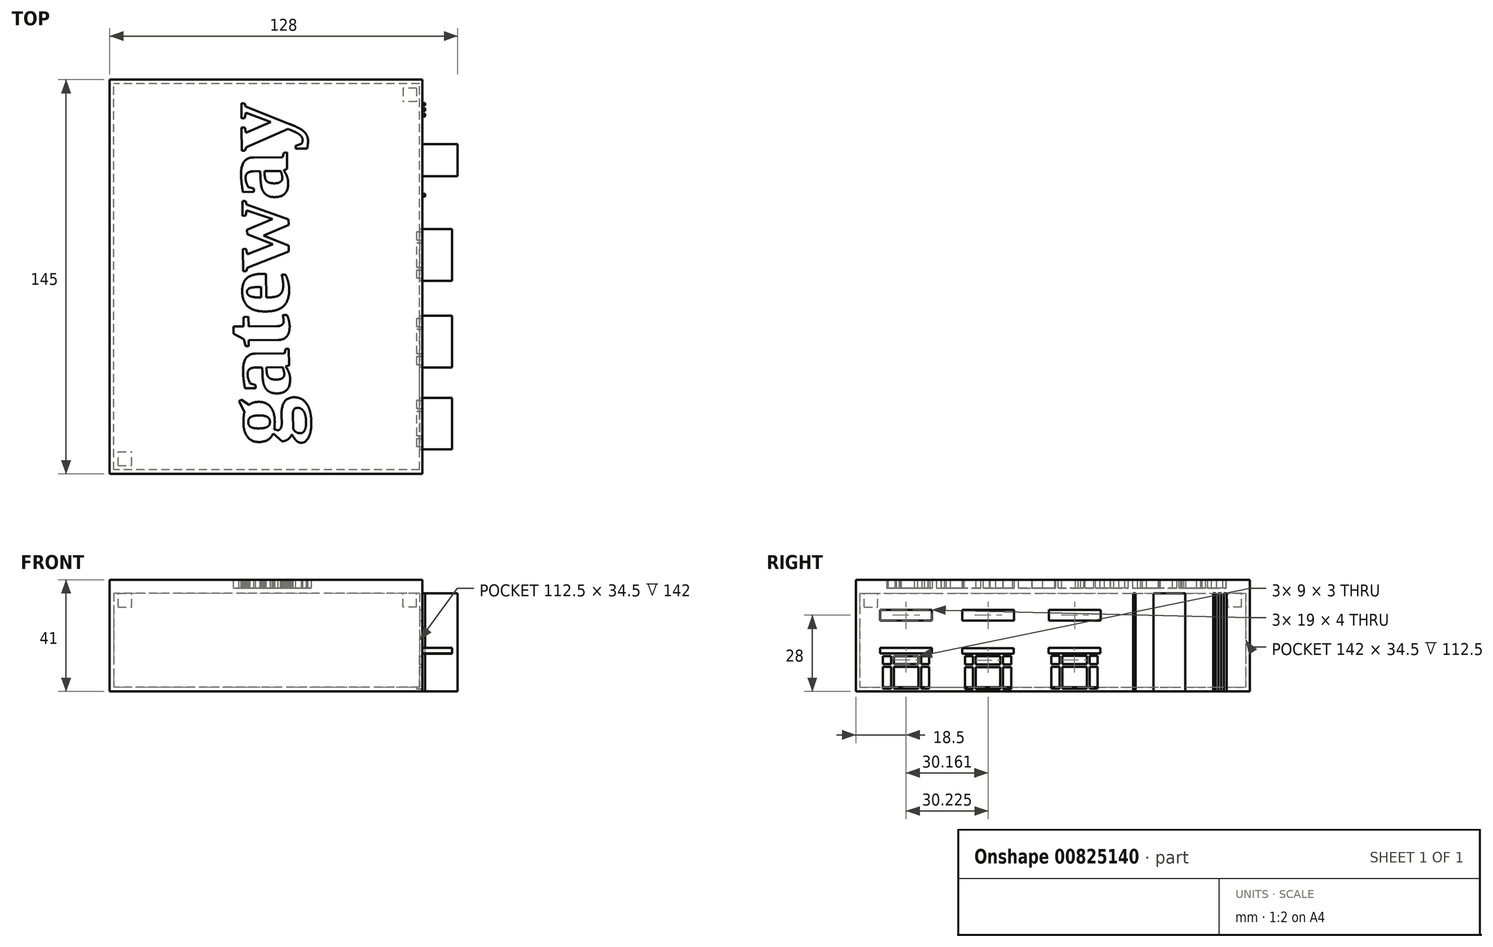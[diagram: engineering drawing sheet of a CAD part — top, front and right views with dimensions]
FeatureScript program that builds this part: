
annotation { "Feature Type Name" : "Feature", "Feature Type Description" : "" }
export const myFeature = defineFeature(function(context is Context, id is Id, definition is map)
    precondition{}
    {
        {
            var Q0;
            Q0=qCreatedBy(makeId("Top.planeOp"),FACE);
            var sketch = newSketch(context, id + "F0", { "sketchPlane" : qUnion([Q0])});
            skLineSegment(sketch, "E0.bottom", {"start": v(0, 0) * mm, "end": v(-116, 0) * mm});
            skLineSegment(sketch, "E0.top", {"start": v(0, 145) * mm, "end": v(-116, 145) * mm});
            skLineSegment(sketch, "E0.left", {"start": v(0, 0) * mm, "end": v(0, 145) * mm});
            skLineSegment(sketch, "E0.right", {"start": v(-116, 0) * mm, "end": v(-116, 145) * mm});
            skSolve(sketch);
        }
        {
            var Q0;
            Q0=makeQuery(id+"F0.imprint","IMPRINT",FACE,{"disambiguationData":[TD([[makeQuery(id+"F0.imprint","IMPRINT",EDGE,{"derivedFrom":sQuery(id+"F0.wireOp",EDGE,"E0.bottom")}),-1.0]])]});
            extrude(context, id + "F1", {"entities" : qUnion([Q0]), "depth" : 36 * mm, "offsetDistance" : 25 * mm});
        }
        {
            var Q0;
            Q0=makeQuery(id+"F1.opExtrude","CAP_FACE",FACE,{"disambiguationData":[OSD([sQuery(id+"F0.wireOp",EDGE,"E0.bottom"),sQuery(id+"F0.wireOp",EDGE,"E0.top"),sQuery(id+"F0.wireOp",EDGE,"E0.left"),sQuery(id+"F0.wireOp",EDGE,"E0.right")])],"isStart":false});
            shell(context, id + "F2", {"entities" : qUnion([Q0]), "thickness" : 3 * mm});
        }
        {
            var Q0;
            Q0=makeQuery(id+"F1.opExtrude","CAP_FACE",FACE,{"disambiguationData":[OSD([sQuery(id+"F0.wireOp",EDGE,"E0.bottom"),sQuery(id+"F0.wireOp",EDGE,"E0.top"),sQuery(id+"F0.wireOp",EDGE,"E0.left"),sQuery(id+"F0.wireOp",EDGE,"E0.right")])],"isStart":false});
            var sketch = newSketch(context, id + "F3", { "sketchPlane" : qUnion([Q0])});
            skLineSegment(sketch, "E1.bottom", {"start": v(-116, 0) * mm, "end": v(0, 0) * mm});
            skLineSegment(sketch, "E1.top", {"start": v(-116, 145) * mm, "end": v(0, 145) * mm});
            skLineSegment(sketch, "E1.left", {"start": v(-116, 0) * mm, "end": v(-116, 145) * mm});
            skLineSegment(sketch, "E1.right", {"start": v(0, 0) * mm, "end": v(0, 145) * mm});
            skSolve(sketch);
        }
        {
            var Q0;
            Q0 = qSketchRegion(id + "F3", true);
            extrude(context, id + "F4", {"entities" : qUnion([Q0]), "depth" : 5 * mm, "offsetDistance" : 25 * mm});
        }
        {
            var Q0;
            Q0=makeQuery(id+"F4.opExtrude","CAP_FACE",FACE,{"disambiguationData":[OSD([sQuery(id+"F3.wireOp",EDGE,"E1.bottom"),sQuery(id+"F3.wireOp",EDGE,"E1.top"),sQuery(id+"F3.wireOp",EDGE,"E1.left"),sQuery(id+"F3.wireOp",EDGE,"E1.right")])],"isStart":false});
            var sketch = newSketch(context, id + "F5", { "sketchPlane" : qUnion([Q0])});
            skLineSegment(sketch, "E2.bottom", {"start": v(-112.9, 3.1) * mm, "end": v(-107.9, 3.1) * mm});
            skLineSegment(sketch, "E2.top", {"start": v(-112.9, 8.1) * mm, "end": v(-107.9, 8.1) * mm});
            skLineSegment(sketch, "E2.left", {"start": v(-112.9, 3.1) * mm, "end": v(-112.9, 8.1) * mm});
            skLineSegment(sketch, "E2.right", {"start": v(-107.9, 3.1) * mm, "end": v(-107.9, 8.1) * mm});
            skSolve(sketch);
        }
        {
            var Q0;
            Q0 = qSketchRegion(id + "F5", true);
            extrude(context, id + "F6", {"entities" : qUnion([Q0]), "operationType" : NewBodyOperationType.ADD, "oppositeDirection" : true, "depth" : 10 * mm, "offsetDistance" : 25 * mm});
        }
        {
            var Q0;
            Q0=makeQuery(id+"F4.opExtrude","CAP_FACE",FACE,{"disambiguationData":[OSD([sQuery(id+"F3.wireOp",EDGE,"E1.bottom"),sQuery(id+"F3.wireOp",EDGE,"E1.top"),sQuery(id+"F3.wireOp",EDGE,"E1.left"),sQuery(id+"F3.wireOp",EDGE,"E1.right")])],"isStart":false});
            var sketch = newSketch(context, id + "F7", { "sketchPlane" : qUnion([Q0])});
            skLineSegment(sketch, "E3.bottom", {"start": v(-3.1, 141.9) * mm, "end": v(-8.1, 141.9) * mm});
            skLineSegment(sketch, "E3.top", {"start": v(-3.1, 136.9) * mm, "end": v(-8.1, 136.9) * mm});
            skLineSegment(sketch, "E3.left", {"start": v(-3.1, 141.9) * mm, "end": v(-3.1, 136.9) * mm});
            skLineSegment(sketch, "E3.right", {"start": v(-8.1, 141.9) * mm, "end": v(-8.1, 136.9) * mm});
            skSolve(sketch);
        }
        {
            var Q0;
            Q0 = qSketchRegion(id + "F7", true);
            extrude(context, id + "F8", {"entities" : qUnion([Q0]), "operationType" : NewBodyOperationType.ADD, "oppositeDirection" : true, "depth" : 10 * mm, "offsetDistance" : 25 * mm});
        }
        {
            var Q0;
            Q0=makeQuery(id+"F4.opExtrude","CAP_FACE",FACE,{"disambiguationData":[OSD([sQuery(id+"F3.wireOp",EDGE,"E1.bottom"),sQuery(id+"F3.wireOp",EDGE,"E1.top"),sQuery(id+"F3.wireOp",EDGE,"E1.left"),sQuery(id+"F3.wireOp",EDGE,"E1.right")])],"isStart":false});
            var sketch = newSketch(context, id + "F9", { "sketchPlane" : qUnion([Q0])});
            skText(sketch, "E4", { "text": "gateway", "fontName": "Tinos-Bold.ttf"});
            const initialGuessF9  = {"E4": [-0.04971, 0.01043, -0.01004, 0.99995, 0.026]};
            skSetInitialGuess(sketch, initialGuessF9);
            skSolve(sketch);
        }
        {
            var Q0;
            Q0 = qSketchRegion(id + "F9", true);
            extrude(context, id + "F10", {"entities" : qUnion([Q0]), "operationType" : NewBodyOperationType.REMOVE, "oppositeDirection" : true, "depth" : 3 * mm, "offsetDistance" : 25 * mm});
        }
        {
            var Q0;
            Q0=makeQuery(id+"F1.opExtrude","SWEPT_FACE",FACE,{"disambiguationData":[OSD([sQuery(id+"F0.wireOp",EDGE,"E0.left")])]});
            var sketch = newSketch(context, id + "F11", { "sketchPlane" : qUnion([Q0])});
            skLineSegment(sketch, "E5.bottom", {"start": v(115, 0) * mm, "end": v(125, 0) * mm});
            skLineSegment(sketch, "E5.top", {"start": v(115, 36) * mm, "end": v(125, 36) * mm});
            skLineSegment(sketch, "E5.left", {"start": v(115, 0) * mm, "end": v(115, 36) * mm});
            skLineSegment(sketch, "E5.right", {"start": v(125, 0) * mm, "end": v(125, 36) * mm});
            skLineSegment(sketch, "E6.bottom", {"start": v(1, 0) * mm, "end": v(2, 0) * mm});
            skLineSegment(sketch, "E6.top", {"start": v(1, 36) * mm, "end": v(2, 36) * mm});
            skLineSegment(sketch, "E6.left", {"start": v(1, 0) * mm, "end": v(1, 36) * mm});
            skLineSegment(sketch, "E6.right", {"start": v(2, 0) * mm, "end": v(2, 36) * mm});
            skLineSegment(sketch, "E7.bottom", {"start": v(3, 0) * mm, "end": v(4, 0) * mm});
            skLineSegment(sketch, "E7.top", {"start": v(3, 36) * mm, "end": v(4, 36) * mm});
            skLineSegment(sketch, "E7.left", {"start": v(3, 0) * mm, "end": v(3, 36) * mm});
            skLineSegment(sketch, "E7.right", {"start": v(4, 0) * mm, "end": v(4, 36) * mm});
            skLineSegment(sketch, "E8.bottom", {"start": v(5, 0) * mm, "end": v(6, 0) * mm});
            skLineSegment(sketch, "E8.top", {"start": v(5, 36) * mm, "end": v(6, 36) * mm});
            skLineSegment(sketch, "E8.left", {"start": v(5, 0) * mm, "end": v(5, 36) * mm});
            skLineSegment(sketch, "E8.right", {"start": v(6, 0) * mm, "end": v(6, 36) * mm});
            skLineSegment(sketch, "E9.bottom", {"start": v(7, 0) * mm, "end": v(8, 0) * mm});
            skLineSegment(sketch, "E9.top", {"start": v(7, 36) * mm, "end": v(8, 36) * mm});
            skLineSegment(sketch, "E9.left", {"start": v(7, 0) * mm, "end": v(7, 36) * mm});
            skLineSegment(sketch, "E9.right", {"start": v(8, 0) * mm, "end": v(8, 36) * mm});
            skSolve(sketch);
        }
        {
            var Q0;
            Q0=makeQuery(id+"F11.imprint","IMPRINT",FACE,{"disambiguationData":[TD([[makeQuery(id+"F11.imprint","IMPRINT",EDGE,{"derivedFrom":sQuery(id+"F11.wireOp",EDGE,"E6.bottom")}),1.0]])]});
            var Q1;
            Q1=makeQuery(id+"F11.imprint","IMPRINT",FACE,{"disambiguationData":[TD([[makeQuery(id+"F11.imprint","IMPRINT",EDGE,{"derivedFrom":sQuery(id+"F11.wireOp",EDGE,"E7.bottom")}),1.0]])]});
            var Q2;
            Q2=makeQuery(id+"F11.imprint","IMPRINT",FACE,{"disambiguationData":[TD([[makeQuery(id+"F11.imprint","IMPRINT",EDGE,{"derivedFrom":sQuery(id+"F11.wireOp",EDGE,"E8.bottom")}),1.0]])]});
            var Q3;
            Q3=makeQuery(id+"F11.imprint","IMPRINT",FACE,{"disambiguationData":[TD([[makeQuery(id+"F11.imprint","IMPRINT",EDGE,{"derivedFrom":sQuery(id+"F11.wireOp",EDGE,"E9.bottom")}),1.0]])]});
            extrude(context, id + "F12", {"entities" : qUnion([Q0, Q1, Q2, Q3]), "operationType" : NewBodyOperationType.REMOVE, "oppositeDirection" : true, "depth" : 1 * mm, "offsetDistance" : 25 * mm});
        }
        {
            var Q0;
            {var subQ1=sQuery(id+"F0.wireOp",EDGE,"E0.left");var subQ2=sQuery(id+"F0.wireOp",EDGE,"E0.top");Q0=makeQuery(id+"F12.boolean.opBoolean","SPLIT",FACE,{"disambiguationData":[TD([makeQuery(id+"F1.opExtrude","SWEPT_FACE",FACE,{"disambiguationData":[OSD([subQ2])]})])],"derivedFrom":makeQuery(id+"F1.opExtrude","SWEPT_FACE",FACE,{"disambiguationData":[OSD([subQ1])]})});}
            var sketch = newSketch(context, id + "F13", { "sketchPlane" : qUnion([Q0])});
            skLineSegment(sketch, "E10.bottom", {"start": v(10, 1) * mm, "end": v(13, 1) * mm});
            skLineSegment(sketch, "E10.top", {"start": v(10, 9) * mm, "end": v(13, 9) * mm});
            skLineSegment(sketch, "E10.left", {"start": v(10, 1) * mm, "end": v(10, 9) * mm});
            skLineSegment(sketch, "E10.right", {"start": v(13, 1) * mm, "end": v(13, 9) * mm});
            skLineSegment(sketch, "E11.bottom", {"start": v(10, 10) * mm, "end": v(13, 10) * mm});
            skLineSegment(sketch, "E11.top", {"start": v(10, 13) * mm, "end": v(13, 13) * mm});
            skLineSegment(sketch, "E11.left", {"start": v(10, 10) * mm, "end": v(10, 13) * mm});
            skLineSegment(sketch, "E11.right", {"start": v(13, 10) * mm, "end": v(13, 13) * mm});
            skLineSegment(sketch, "E12.bottom", {"start": v(14, 1) * mm, "end": v(23, 1) * mm});
            skLineSegment(sketch, "E12.top", {"start": v(14, 9) * mm, "end": v(23, 9) * mm});
            skLineSegment(sketch, "E12.left", {"start": v(14, 1) * mm, "end": v(14, 9) * mm});
            skLineSegment(sketch, "E12.right", {"start": v(23, 1) * mm, "end": v(23, 9) * mm});
            skLineSegment(sketch, "E13.bottom", {"start": v(23, 10) * mm, "end": v(14, 10) * mm});
            skLineSegment(sketch, "E13.top", {"start": v(23, 13) * mm, "end": v(14, 13) * mm});
            skLineSegment(sketch, "E13.left", {"start": v(23, 10) * mm, "end": v(23, 13) * mm});
            skLineSegment(sketch, "E13.right", {"start": v(14, 10) * mm, "end": v(14, 13) * mm});
            skLineSegment(sketch, "E14.bottom", {"start": v(24, 1) * mm, "end": v(27, 1) * mm});
            skLineSegment(sketch, "E14.top", {"start": v(24, 9) * mm, "end": v(27, 9) * mm});
            skLineSegment(sketch, "E14.left", {"start": v(24, 1) * mm, "end": v(24, 9) * mm});
            skLineSegment(sketch, "E14.right", {"start": v(27, 1) * mm, "end": v(27, 9) * mm});
            skLineSegment(sketch, "E15.bottom", {"start": v(24, 10) * mm, "end": v(27, 10) * mm});
            skLineSegment(sketch, "E15.top", {"start": v(24, 13) * mm, "end": v(27, 13) * mm});
            skLineSegment(sketch, "E15.left", {"start": v(24, 10) * mm, "end": v(24, 13) * mm});
            skLineSegment(sketch, "E15.right", {"start": v(27, 10) * mm, "end": v(27, 13) * mm});
            skLineSegment(sketch, "E16.bottom", {"start": v(9, 14) * mm, "end": v(28, 14) * mm});
            skLineSegment(sketch, "E16.top", {"start": v(9, 16) * mm, "end": v(28, 16) * mm});
            skLineSegment(sketch, "E16.left", {"start": v(9, 14) * mm, "end": v(9, 16) * mm});
            skLineSegment(sketch, "E16.right", {"start": v(28, 14) * mm, "end": v(28, 16) * mm});
            skLineSegment(sketch, "E17.bottom", {"start": v(40.16, 0.88) * mm, "end": v(43.16, 0.88) * mm});
            skLineSegment(sketch, "E17.top", {"start": v(40.16, 8.88) * mm, "end": v(43.16, 8.88) * mm});
            skLineSegment(sketch, "E17.left", {"start": v(40.16, 0.88) * mm, "end": v(40.16, 8.88) * mm});
            skLineSegment(sketch, "E17.right", {"start": v(43.16, 0.88) * mm, "end": v(43.16, 8.88) * mm});
            skLineSegment(sketch, "E18.bottom", {"start": v(40.16, 9.88) * mm, "end": v(43.16, 9.88) * mm});
            skLineSegment(sketch, "E18.top", {"start": v(40.16, 12.88) * mm, "end": v(43.16, 12.88) * mm});
            skLineSegment(sketch, "E18.left", {"start": v(40.16, 9.88) * mm, "end": v(40.16, 12.88) * mm});
            skLineSegment(sketch, "E18.right", {"start": v(43.16, 9.88) * mm, "end": v(43.16, 12.88) * mm});
            skLineSegment(sketch, "E19.bottom", {"start": v(44.16, 0.88) * mm, "end": v(53.16, 0.88) * mm});
            skLineSegment(sketch, "E19.top", {"start": v(44.16, 8.89) * mm, "end": v(53.16, 8.89) * mm});
            skLineSegment(sketch, "E19.left", {"start": v(44.16, 0.88) * mm, "end": v(44.16, 8.89) * mm});
            skLineSegment(sketch, "E19.right", {"start": v(53.16, 0.88) * mm, "end": v(53.16, 8.89) * mm});
            skLineSegment(sketch, "E20.bottom", {"start": v(53.16, 9.88) * mm, "end": v(44.16, 9.88) * mm});
            skLineSegment(sketch, "E20.top", {"start": v(53.16, 12.88) * mm, "end": v(44.16, 12.88) * mm});
            skLineSegment(sketch, "E20.left", {"start": v(53.16, 9.88) * mm, "end": v(53.16, 12.88) * mm});
            skLineSegment(sketch, "E20.right", {"start": v(44.16, 9.88) * mm, "end": v(44.16, 12.88) * mm});
            skLineSegment(sketch, "E21.bottom", {"start": v(54.16, 0.88) * mm, "end": v(57.19, 0.88) * mm});
            skLineSegment(sketch, "E21.top", {"start": v(54.16, 8.88) * mm, "end": v(57.19, 8.88) * mm});
            skLineSegment(sketch, "E21.left", {"start": v(54.16, 0.88) * mm, "end": v(54.16, 8.88) * mm});
            skLineSegment(sketch, "E21.right", {"start": v(57.19, 0.88) * mm, "end": v(57.19, 8.88) * mm});
            skLineSegment(sketch, "E22.bottom", {"start": v(54.16, 9.88) * mm, "end": v(57.16, 9.88) * mm});
            skLineSegment(sketch, "E22.top", {"start": v(54.16, 12.88) * mm, "end": v(57.16, 12.88) * mm});
            skLineSegment(sketch, "E22.left", {"start": v(54.16, 9.88) * mm, "end": v(54.16, 12.88) * mm});
            skLineSegment(sketch, "E22.right", {"start": v(57.16, 9.88) * mm, "end": v(57.16, 12.88) * mm});
            skLineSegment(sketch, "E23.bottom", {"start": v(39.16, 13.88) * mm, "end": v(58.16, 13.88) * mm});
            skLineSegment(sketch, "E23.top", {"start": v(39.16, 15.88) * mm, "end": v(58.16, 15.88) * mm});
            skLineSegment(sketch, "E23.left", {"start": v(39.16, 13.88) * mm, "end": v(39.16, 15.88) * mm});
            skLineSegment(sketch, "E23.right", {"start": v(58.16, 13.88) * mm, "end": v(58.16, 15.88) * mm});
            skLineSegment(sketch, "E24.bottom", {"start": v(71.98, 1.01) * mm, "end": v(74.98, 1.01) * mm});
            skLineSegment(sketch, "E24.top", {"start": v(71.98, 9.01) * mm, "end": v(74.98, 9.01) * mm});
            skLineSegment(sketch, "E24.left", {"start": v(71.98, 1.01) * mm, "end": v(71.98, 9.01) * mm});
            skLineSegment(sketch, "E24.right", {"start": v(74.98, 1.01) * mm, "end": v(74.98, 9.01) * mm});
            skLineSegment(sketch, "E25.bottom", {"start": v(71.98, 10.01) * mm, "end": v(74.98, 10.01) * mm});
            skLineSegment(sketch, "E25.top", {"start": v(71.98, 13.01) * mm, "end": v(74.98, 13.01) * mm});
            skLineSegment(sketch, "E25.left", {"start": v(71.98, 10.01) * mm, "end": v(71.98, 13.01) * mm});
            skLineSegment(sketch, "E25.right", {"start": v(74.98, 10.01) * mm, "end": v(74.98, 13.01) * mm});
            skLineSegment(sketch, "E26.bottom", {"start": v(75.98, 1.01) * mm, "end": v(84.98, 1.01) * mm});
            skLineSegment(sketch, "E26.top", {"start": v(75.98, 9.02) * mm, "end": v(84.98, 9.02) * mm});
            skLineSegment(sketch, "E26.left", {"start": v(75.98, 1.01) * mm, "end": v(75.98, 9.02) * mm});
            skLineSegment(sketch, "E26.right", {"start": v(84.98, 1.01) * mm, "end": v(84.98, 9.02) * mm});
            skLineSegment(sketch, "E27.bottom", {"start": v(84.98, 10.01) * mm, "end": v(75.98, 10.01) * mm});
            skLineSegment(sketch, "E27.top", {"start": v(84.98, 13.01) * mm, "end": v(75.98, 13.01) * mm});
            skLineSegment(sketch, "E27.left", {"start": v(84.98, 10.01) * mm, "end": v(84.98, 13.01) * mm});
            skLineSegment(sketch, "E27.right", {"start": v(75.98, 10.01) * mm, "end": v(75.98, 13.01) * mm});
            skLineSegment(sketch, "E28.bottom", {"start": v(85.98, 1.01) * mm, "end": v(89.01, 1.01) * mm});
            skLineSegment(sketch, "E28.top", {"start": v(85.98, 9.01) * mm, "end": v(89.01, 9.01) * mm});
            skLineSegment(sketch, "E28.left", {"start": v(85.98, 1.01) * mm, "end": v(85.98, 9.01) * mm});
            skLineSegment(sketch, "E28.right", {"start": v(89.01, 1.01) * mm, "end": v(89.01, 9.01) * mm});
            skLineSegment(sketch, "E29.bottom", {"start": v(85.98, 10.01) * mm, "end": v(88.98, 10.01) * mm});
            skLineSegment(sketch, "E29.top", {"start": v(85.98, 13.01) * mm, "end": v(88.98, 13.01) * mm});
            skLineSegment(sketch, "E29.left", {"start": v(85.98, 10.01) * mm, "end": v(85.98, 13.01) * mm});
            skLineSegment(sketch, "E29.right", {"start": v(88.98, 10.01) * mm, "end": v(88.98, 13.01) * mm});
            skLineSegment(sketch, "E30.bottom", {"start": v(70.98, 14.01) * mm, "end": v(89.98, 14.01) * mm});
            skLineSegment(sketch, "E30.top", {"start": v(70.98, 16.01) * mm, "end": v(89.98, 16.01) * mm});
            skLineSegment(sketch, "E30.left", {"start": v(70.98, 14.01) * mm, "end": v(70.98, 16.01) * mm});
            skLineSegment(sketch, "E30.right", {"start": v(89.98, 14.01) * mm, "end": v(89.98, 16.01) * mm});
            skLineSegment(sketch, "E31.bottom", {"start": v(109.5, 0) * mm, "end": v(121.28, 0) * mm});
            skLineSegment(sketch, "E31.top", {"start": v(109.5, 36) * mm, "end": v(121.28, 36) * mm});
            skLineSegment(sketch, "E31.left", {"start": v(109.5, 0) * mm, "end": v(109.5, 36) * mm});
            skLineSegment(sketch, "E31.right", {"start": v(121.28, 0) * mm, "end": v(121.28, 36) * mm});
            skSolve(sketch);
        }
        {
            var Q0;
            Q0=makeQuery(id+"F13.imprint","IMPRINT",FACE,{"disambiguationData":[TD([[makeQuery(id+"F13.imprint","IMPRINT",EDGE,{"derivedFrom":sQuery(id+"F13.wireOp",EDGE,"E11.bottom")}),1.0]])]});
            var Q1;
            Q1=makeQuery(id+"F13.imprint","IMPRINT",FACE,{"disambiguationData":[TD([[makeQuery(id+"F13.imprint","IMPRINT",EDGE,{"derivedFrom":sQuery(id+"F13.wireOp",EDGE,"E13.bottom")}),-1.0]])]});
            var Q2;
            Q2=makeQuery(id+"F13.imprint","IMPRINT",FACE,{"disambiguationData":[TD([[makeQuery(id+"F13.imprint","IMPRINT",EDGE,{"derivedFrom":sQuery(id+"F13.wireOp",EDGE,"E15.bottom")}),1.0]])]});
            var Q3;
            Q3=makeQuery(id+"F13.imprint","IMPRINT",FACE,{"disambiguationData":[TD([[makeQuery(id+"F13.imprint","IMPRINT",EDGE,{"derivedFrom":sQuery(id+"F13.wireOp",EDGE,"E14.bottom")}),1.0]])]});
            var Q4;
            Q4=makeQuery(id+"F13.imprint","IMPRINT",FACE,{"disambiguationData":[TD([[makeQuery(id+"F13.imprint","IMPRINT",EDGE,{"derivedFrom":sQuery(id+"F13.wireOp",EDGE,"E12.bottom")}),1.0]])]});
            var Q5;
            Q5=makeQuery(id+"F13.imprint","IMPRINT",FACE,{"disambiguationData":[TD([[makeQuery(id+"F13.imprint","IMPRINT",EDGE,{"derivedFrom":sQuery(id+"F13.wireOp",EDGE,"E10.bottom")}),1.0]])]});
            var Q6;
            Q6=makeQuery(id+"F13.imprint","IMPRINT",FACE,{"disambiguationData":[TD([[makeQuery(id+"F13.imprint","IMPRINT",EDGE,{"derivedFrom":sQuery(id+"F13.wireOp",EDGE,"E18.bottom")}),1.0]])]});
            var Q7;
            Q7=makeQuery(id+"F13.imprint","IMPRINT",FACE,{"disambiguationData":[TD([[makeQuery(id+"F13.imprint","IMPRINT",EDGE,{"derivedFrom":sQuery(id+"F13.wireOp",EDGE,"E20.bottom")}),-1.0]])]});
            var Q8;
            Q8=makeQuery(id+"F13.imprint","IMPRINT",FACE,{"disambiguationData":[TD([[makeQuery(id+"F13.imprint","IMPRINT",EDGE,{"derivedFrom":sQuery(id+"F13.wireOp",EDGE,"E22.bottom")}),1.0]])]});
            var Q9;
            Q9=makeQuery(id+"F13.imprint","IMPRINT",FACE,{"disambiguationData":[TD([[makeQuery(id+"F13.imprint","IMPRINT",EDGE,{"derivedFrom":sQuery(id+"F13.wireOp",EDGE,"E21.bottom")}),1.0]])]});
            var Q10;
            Q10=makeQuery(id+"F13.imprint","IMPRINT",FACE,{"disambiguationData":[TD([[makeQuery(id+"F13.imprint","IMPRINT",EDGE,{"derivedFrom":sQuery(id+"F13.wireOp",EDGE,"E19.bottom")}),1.0]])]});
            var Q11;
            Q11=makeQuery(id+"F13.imprint","IMPRINT",FACE,{"disambiguationData":[TD([[makeQuery(id+"F13.imprint","IMPRINT",EDGE,{"derivedFrom":sQuery(id+"F13.wireOp",EDGE,"E17.bottom")}),1.0]])]});
            var Q12;
            Q12=makeQuery(id+"F13.imprint","IMPRINT",FACE,{"disambiguationData":[TD([[makeQuery(id+"F13.imprint","IMPRINT",EDGE,{"derivedFrom":sQuery(id+"F13.wireOp",EDGE,"E25.bottom")}),1.0]])]});
            var Q13;
            Q13=makeQuery(id+"F13.imprint","IMPRINT",FACE,{"disambiguationData":[TD([[makeQuery(id+"F13.imprint","IMPRINT",EDGE,{"derivedFrom":sQuery(id+"F13.wireOp",EDGE,"E27.bottom")}),-1.0]])]});
            var Q14;
            Q14=makeQuery(id+"F13.imprint","IMPRINT",FACE,{"disambiguationData":[TD([[makeQuery(id+"F13.imprint","IMPRINT",EDGE,{"derivedFrom":sQuery(id+"F13.wireOp",EDGE,"E29.bottom")}),1.0]])]});
            var Q15;
            Q15=makeQuery(id+"F13.imprint","IMPRINT",FACE,{"disambiguationData":[TD([[makeQuery(id+"F13.imprint","IMPRINT",EDGE,{"derivedFrom":sQuery(id+"F13.wireOp",EDGE,"E28.bottom")}),1.0]])]});
            var Q16;
            Q16=makeQuery(id+"F13.imprint","IMPRINT",FACE,{"disambiguationData":[TD([[makeQuery(id+"F13.imprint","IMPRINT",EDGE,{"derivedFrom":sQuery(id+"F13.wireOp",EDGE,"E26.bottom")}),1.0]])]});
            var Q17;
            Q17=makeQuery(id+"F13.imprint","IMPRINT",FACE,{"disambiguationData":[TD([[makeQuery(id+"F13.imprint","IMPRINT",EDGE,{"derivedFrom":sQuery(id+"F13.wireOp",EDGE,"E24.bottom")}),1.0]])]});
            extrude(context, id + "F14", {"entities" : qUnion([Q0, Q1, Q2, Q3, Q4, Q5, Q6, Q7, Q8, Q9, Q10, Q11, Q12, Q13, Q14, Q15, Q16, Q17]), "operationType" : NewBodyOperationType.REMOVE, "oppositeDirection" : true, "depth" : 3 * mm, "offsetDistance" : 25 * mm});
        }
        {
            var Q0;
            Q0=makeQuery(id+"F13.imprint","IMPRINT",FACE,{"disambiguationData":[TD([[makeQuery(id+"F13.imprint","IMPRINT",EDGE,{"derivedFrom":sQuery(id+"F13.wireOp",EDGE,"E30.bottom")}),1.0]])]});
            var Q1;
            Q1=makeQuery(id+"F13.imprint","IMPRINT",FACE,{"disambiguationData":[TD([[makeQuery(id+"F13.imprint","IMPRINT",EDGE,{"derivedFrom":sQuery(id+"F13.wireOp",EDGE,"E23.bottom")}),1.0]])]});
            var Q2;
            Q2=makeQuery(id+"F13.imprint","IMPRINT",FACE,{"disambiguationData":[TD([[makeQuery(id+"F13.imprint","IMPRINT",EDGE,{"derivedFrom":sQuery(id+"F13.wireOp",EDGE,"E16.bottom")}),1.0]])]});
            extrude(context, id + "F15", {"entities" : qUnion([Q0, Q1, Q2]), "operationType" : NewBodyOperationType.ADD, "depth" : 10 * mm, "offsetDistance" : 25 * mm});
        }
        {
            var Q0;
            Q0=makeQuery(id+"F13.imprint","IMPRINT",FACE,{"disambiguationData":[TD([[makeQuery(id+"F13.imprint","IMPRINT",EDGE,{"derivedFrom":sQuery(id+"F13.wireOp",EDGE,"E31.bottom")}),1.0]])]});
            extrude(context, id + "F16", {"entities" : qUnion([Q0]), "operationType" : NewBodyOperationType.ADD, "depth" : 12 * mm, "offsetDistance" : 25 * mm});
        }
        {
            var Q0;
            {var subQ0=makeQuery(id+"F12.opExtrude","SWEPT_FACE",FACE,{"disambiguationData":[OSD([sQuery(id+"F11.wireOp",EDGE,"E9.right")])]});var subQ2=sQuery(id+"F0.wireOp",EDGE,"E0.left");var subQ3=sQuery(id+"F0.wireOp",EDGE,"E0.top");Q0=makeQuery(id+"F16.boolean.opBoolean","SPLIT",FACE,{"disambiguationData":[TD([makeQuery(id+"F12.boolean.opBoolean","COPY",FACE,{"derivedFrom":subQ0})])],"derivedFrom":makeQuery(id+"F12.boolean.opBoolean","SPLIT",FACE,{"disambiguationData":[TD([makeQuery(id+"F1.opExtrude","SWEPT_FACE",FACE,{"disambiguationData":[OSD([subQ3])]})])],"derivedFrom":makeQuery(id+"F1.opExtrude","SWEPT_FACE",FACE,{"disambiguationData":[OSD([subQ2])]})})});}
            var sketch = newSketch(context, id + "F17", { "sketchPlane" : qUnion([Q0])});
            skLineSegment(sketch, "E32.bottom", {"start": v(30.5, 0) * mm, "end": v(31.5, 0) * mm});
            skLineSegment(sketch, "E32.top", {"start": v(30.5, 36) * mm, "end": v(31.5, 36) * mm});
            skLineSegment(sketch, "E32.left", {"start": v(30.5, 0) * mm, "end": v(30.5, 36) * mm});
            skLineSegment(sketch, "E32.right", {"start": v(31.5, 0) * mm, "end": v(31.5, 36) * mm});
            skLineSegment(sketch, "E33.bottom", {"start": v(32.5, 0) * mm, "end": v(33.5, 0) * mm});
            skLineSegment(sketch, "E33.top", {"start": v(32.5, 36) * mm, "end": v(33.5, 36) * mm});
            skLineSegment(sketch, "E33.left", {"start": v(32.5, 0) * mm, "end": v(32.5, 36) * mm});
            skLineSegment(sketch, "E33.right", {"start": v(33.5, 0) * mm, "end": v(33.5, 36) * mm});
            skLineSegment(sketch, "E34.bottom", {"start": v(34.5, 0) * mm, "end": v(35.5, 0) * mm});
            skLineSegment(sketch, "E34.top", {"start": v(34.5, 36) * mm, "end": v(35.5, 36) * mm});
            skLineSegment(sketch, "E34.left", {"start": v(34.5, 0) * mm, "end": v(34.5, 36) * mm});
            skLineSegment(sketch, "E34.right", {"start": v(35.5, 0) * mm, "end": v(35.5, 36) * mm});
            skLineSegment(sketch, "E35.bottom", {"start": v(36.5, 0) * mm, "end": v(37.5, 0) * mm});
            skLineSegment(sketch, "E35.top", {"start": v(36.5, 36) * mm, "end": v(37.5, 36) * mm});
            skLineSegment(sketch, "E35.left", {"start": v(36.5, 0) * mm, "end": v(36.5, 36) * mm});
            skLineSegment(sketch, "E35.right", {"start": v(37.5, 0) * mm, "end": v(37.5, 36) * mm});
            skLineSegment(sketch, "E36.bottom", {"start": v(60.98, 0) * mm, "end": v(61.98, 0) * mm});
            skLineSegment(sketch, "E36.top", {"start": v(60.98, 36) * mm, "end": v(61.98, 36) * mm});
            skLineSegment(sketch, "E36.left", {"start": v(60.98, 0) * mm, "end": v(60.98, 36) * mm});
            skLineSegment(sketch, "E36.right", {"start": v(61.98, 0) * mm, "end": v(61.98, 36) * mm});
            skLineSegment(sketch, "E37.bottom", {"start": v(62.98, 0) * mm, "end": v(63.98, 0) * mm});
            skLineSegment(sketch, "E37.top", {"start": v(62.98, 36) * mm, "end": v(63.98, 36) * mm});
            skLineSegment(sketch, "E37.left", {"start": v(62.98, 0) * mm, "end": v(62.98, 36) * mm});
            skLineSegment(sketch, "E37.right", {"start": v(63.98, 0) * mm, "end": v(63.98, 36) * mm});
            skLineSegment(sketch, "E38.bottom", {"start": v(64.98, 0) * mm, "end": v(65.98, 0) * mm});
            skLineSegment(sketch, "E38.top", {"start": v(64.98, 36) * mm, "end": v(65.98, 36) * mm});
            skLineSegment(sketch, "E38.left", {"start": v(64.98, 0) * mm, "end": v(64.98, 36) * mm});
            skLineSegment(sketch, "E38.right", {"start": v(65.98, 0) * mm, "end": v(65.98, 36) * mm});
            skLineSegment(sketch, "E39.bottom", {"start": v(66.98, 0) * mm, "end": v(67.98, 0) * mm});
            skLineSegment(sketch, "E39.top", {"start": v(66.98, 36) * mm, "end": v(67.98, 36) * mm});
            skLineSegment(sketch, "E39.left", {"start": v(66.98, 0) * mm, "end": v(66.98, 36) * mm});
            skLineSegment(sketch, "E39.right", {"start": v(67.98, 0) * mm, "end": v(67.98, 36) * mm});
            skLineSegment(sketch, "E40.MirrorCS", {"start": v(98.98, 0) * mm, "end": v(97.98, 0) * mm});
            skLineSegment(sketch, "E41.MirrorCS", {"start": v(96.98, 0) * mm, "end": v(95.98, 0) * mm});
            skLineSegment(sketch, "E42.MirrorCS", {"start": v(100.98, 0) * mm, "end": v(99.98, 0) * mm});
            skLineSegment(sketch, "E43.MirrorCS", {"start": v(96.98, 36) * mm, "end": v(95.98, 36) * mm});
            skLineSegment(sketch, "E44.MirrorCS", {"start": v(100.98, 36) * mm, "end": v(99.98, 36) * mm});
            skLineSegment(sketch, "E45.MirrorCS", {"start": v(102.98, 36) * mm, "end": v(101.98, 36) * mm});
            skLineSegment(sketch, "E46.MirrorCS", {"start": v(102.98, 0) * mm, "end": v(101.98, 0) * mm});
            skLineSegment(sketch, "E47.MirrorCS", {"start": v(98.98, 36) * mm, "end": v(97.98, 36) * mm});
            skLineSegment(sketch, "E48.MirrorCS", {"start": v(97.98, 0) * mm, "end": v(97.98, 36) * mm});
            skLineSegment(sketch, "E49.MirrorCS", {"start": v(102.98, 0) * mm, "end": v(102.98, 36) * mm});
            skLineSegment(sketch, "E50.MirrorCS", {"start": v(99.98, 0) * mm, "end": v(99.98, 36) * mm});
            skLineSegment(sketch, "E51.MirrorCS", {"start": v(98.98, 0) * mm, "end": v(98.98, 36) * mm});
            skLineSegment(sketch, "E52.MirrorCS", {"start": v(95.98, 0) * mm, "end": v(95.98, 36) * mm});
            skLineSegment(sketch, "E53.MirrorCS", {"start": v(96.98, 0) * mm, "end": v(96.98, 36) * mm});
            skLineSegment(sketch, "E54.MirrorCS", {"start": v(101.98, 0) * mm, "end": v(101.98, 36) * mm});
            skLineSegment(sketch, "E55.MirrorCS", {"start": v(100.98, 0) * mm, "end": v(100.98, 36) * mm});
            skLineSegment(sketch, "E56.MirrorCS", {"start": v(134.46, 0) * mm, "end": v(133.46, 0) * mm});
            skLineSegment(sketch, "E57.MirrorCS", {"start": v(132.46, 0) * mm, "end": v(131.46, 0) * mm});
            skLineSegment(sketch, "E58.MirrorCS", {"start": v(136.46, 0) * mm, "end": v(135.46, 0) * mm});
            skLineSegment(sketch, "E59.MirrorCS", {"start": v(132.46, 36) * mm, "end": v(131.46, 36) * mm});
            skLineSegment(sketch, "E60.MirrorCS", {"start": v(136.46, 36) * mm, "end": v(135.46, 36) * mm});
            skLineSegment(sketch, "E61.MirrorCS", {"start": v(138.46, 36) * mm, "end": v(137.46, 36) * mm});
            skLineSegment(sketch, "E62.MirrorCS", {"start": v(138.46, 0) * mm, "end": v(137.46, 0) * mm});
            skLineSegment(sketch, "E63.MirrorCS", {"start": v(134.46, 36) * mm, "end": v(133.46, 36) * mm});
            skLineSegment(sketch, "E64.MirrorCS", {"start": v(133.46, 0) * mm, "end": v(133.46, 36) * mm});
            skLineSegment(sketch, "E65.MirrorCS", {"start": v(138.46, 0) * mm, "end": v(138.46, 36) * mm});
            skLineSegment(sketch, "E66.MirrorCS", {"start": v(135.46, 0) * mm, "end": v(135.46, 36) * mm});
            skLineSegment(sketch, "E67.MirrorCS", {"start": v(134.46, 0) * mm, "end": v(134.46, 36) * mm});
            skLineSegment(sketch, "E68.MirrorCS", {"start": v(131.46, 0) * mm, "end": v(131.46, 36) * mm});
            skLineSegment(sketch, "E69.MirrorCS", {"start": v(132.46, 0) * mm, "end": v(132.46, 36) * mm});
            skLineSegment(sketch, "E70.MirrorCS", {"start": v(137.46, 0) * mm, "end": v(137.46, 36) * mm});
            skLineSegment(sketch, "E71.MirrorCS", {"start": v(136.46, 0) * mm, "end": v(136.46, 36) * mm});
            skSolve(sketch);
        }
        {
            var Q0;
            Q0=makeQuery(id+"F17.imprint","IMPRINT",FACE,{"disambiguationData":[TD([[makeQuery(id+"F17.imprint","IMPRINT",EDGE,{"derivedFrom":sQuery(id+"F17.wireOp",EDGE,"E32.bottom")}),1.0]])]});
            var Q1;
            Q1=makeQuery(id+"F17.imprint","IMPRINT",FACE,{"disambiguationData":[TD([[makeQuery(id+"F17.imprint","IMPRINT",EDGE,{"derivedFrom":sQuery(id+"F17.wireOp",EDGE,"E33.bottom")}),1.0]])]});
            var Q2;
            Q2=makeQuery(id+"F17.imprint","IMPRINT",FACE,{"disambiguationData":[TD([[makeQuery(id+"F17.imprint","IMPRINT",EDGE,{"derivedFrom":sQuery(id+"F17.wireOp",EDGE,"E34.bottom")}),1.0]])]});
            var Q3;
            Q3=makeQuery(id+"F17.imprint","IMPRINT",FACE,{"disambiguationData":[TD([[makeQuery(id+"F17.imprint","IMPRINT",EDGE,{"derivedFrom":sQuery(id+"F17.wireOp",EDGE,"E35.bottom")}),1.0]])]});
            var Q4;
            Q4=makeQuery(id+"F17.imprint","IMPRINT",FACE,{"disambiguationData":[TD([[makeQuery(id+"F17.imprint","IMPRINT",EDGE,{"derivedFrom":sQuery(id+"F17.wireOp",EDGE,"E36.bottom")}),1.0]])]});
            var Q5;
            Q5=makeQuery(id+"F17.imprint","IMPRINT",FACE,{"disambiguationData":[TD([[makeQuery(id+"F17.imprint","IMPRINT",EDGE,{"derivedFrom":sQuery(id+"F17.wireOp",EDGE,"E37.bottom")}),1.0]])]});
            var Q6;
            Q6=makeQuery(id+"F17.imprint","IMPRINT",FACE,{"disambiguationData":[TD([[makeQuery(id+"F17.imprint","IMPRINT",EDGE,{"derivedFrom":sQuery(id+"F17.wireOp",EDGE,"E38.bottom")}),1.0]])]});
            var Q7;
            Q7=makeQuery(id+"F17.imprint","IMPRINT",FACE,{"disambiguationData":[TD([[makeQuery(id+"F17.imprint","IMPRINT",EDGE,{"derivedFrom":sQuery(id+"F17.wireOp",EDGE,"E39.bottom")}),1.0]])]});
            extrude(context, id + "F18", {"entities" : qUnion([Q0, Q1, Q2, Q3, Q4, Q5, Q6, Q7]), "operationType" : NewBodyOperationType.REMOVE, "oppositeDirection" : true, "depth" : 1 * mm, "offsetDistance" : 25 * mm});
        }
        {
            var Q0;
            Q0=makeQuery(id+"F17.imprint","IMPRINT",FACE,{"disambiguationData":[TD([[makeQuery(id+"F17.imprint","IMPRINT",EDGE,{"derivedFrom":sQuery(id+"F17.wireOp",EDGE,"E41.MirrorCS")}),1.0]])]});
            var Q1;
            Q1=makeQuery(id+"F17.imprint","IMPRINT",FACE,{"disambiguationData":[TD([[makeQuery(id+"F17.imprint","IMPRINT",EDGE,{"derivedFrom":sQuery(id+"F17.wireOp",EDGE,"E40.MirrorCS")}),1.0]])]});
            var Q2;
            Q2=makeQuery(id+"F17.imprint","IMPRINT",FACE,{"disambiguationData":[TD([[makeQuery(id+"F17.imprint","IMPRINT",EDGE,{"derivedFrom":sQuery(id+"F17.wireOp",EDGE,"E42.MirrorCS")}),1.0]])]});
            var Q3;
            Q3=makeQuery(id+"F17.imprint","IMPRINT",FACE,{"disambiguationData":[TD([[makeQuery(id+"F17.imprint","IMPRINT",EDGE,{"derivedFrom":sQuery(id+"F17.wireOp",EDGE,"E45.MirrorCS")}),-1.0]])]});
            var Q4;
            Q4=makeQuery(id+"F17.imprint","IMPRINT",FACE,{"disambiguationData":[TD([[makeQuery(id+"F17.imprint","IMPRINT",EDGE,{"derivedFrom":sQuery(id+"F17.wireOp",EDGE,"E57.MirrorCS")}),-1.0]])]});
            var Q5;
            Q5=makeQuery(id+"F17.imprint","IMPRINT",FACE,{"disambiguationData":[TD([[makeQuery(id+"F17.imprint","IMPRINT",EDGE,{"derivedFrom":sQuery(id+"F17.wireOp",EDGE,"E56.MirrorCS")}),-1.0]])]});
            var Q6;
            Q6=makeQuery(id+"F17.imprint","IMPRINT",FACE,{"disambiguationData":[TD([[makeQuery(id+"F17.imprint","IMPRINT",EDGE,{"derivedFrom":sQuery(id+"F17.wireOp",EDGE,"E58.MirrorCS")}),-1.0]])]});
            var Q7;
            Q7=makeQuery(id+"F17.imprint","IMPRINT",FACE,{"disambiguationData":[TD([[makeQuery(id+"F17.imprint","IMPRINT",EDGE,{"derivedFrom":sQuery(id+"F17.wireOp",EDGE,"E61.MirrorCS")}),1.0]])]});
            extrude(context, id + "F19", {"entities" : qUnion([Q0, Q1, Q2, Q3, Q4, Q5, Q6, Q7]), "operationType" : NewBodyOperationType.REMOVE, "oppositeDirection" : true, "depth" : 1 * mm, "offsetDistance" : 25 * mm});
        }
        {
            var Q0;
            {var subQ6=sQuery(id+"F0.wireOp",EDGE,"E0.left");var subQ7=sQuery(id+"F0.wireOp",EDGE,"E0.top");var subQ18=makeQuery(id+"F12.opExtrude","SWEPT_FACE",FACE,{"disambiguationData":[OSD([sQuery(id+"F11.wireOp",EDGE,"E9.right")])]});var subQ19=makeQuery(id+"F12.boolean.opBoolean","COPY",FACE,{"derivedFrom":subQ18});Q0=makeQuery(id+"F18.boolean.opBoolean","SPLIT",FACE,{"disambiguationData":[TD([subQ19])],"derivedFrom":makeQuery(id+"F16.boolean.opBoolean","SPLIT",FACE,{"disambiguationData":[TD([subQ19])],"derivedFrom":makeQuery(id+"F12.boolean.opBoolean","SPLIT",FACE,{"disambiguationData":[TD([makeQuery(id+"F1.opExtrude","SWEPT_FACE",FACE,{"disambiguationData":[OSD([subQ7])]})])],"derivedFrom":makeQuery(id+"F1.opExtrude","SWEPT_FACE",FACE,{"disambiguationData":[OSD([subQ6])]})})})});}
            var sketch = newSketch(context, id + "F20", { "sketchPlane" : qUnion([Q0])});
            skLineSegment(sketch, "E72.bottom", {"start": v(9, 26) * mm, "end": v(28, 26) * mm});
            skLineSegment(sketch, "E72.top", {"start": v(9, 30) * mm, "end": v(28, 30) * mm});
            skLineSegment(sketch, "E72.left", {"start": v(9, 26) * mm, "end": v(9, 30) * mm});
            skLineSegment(sketch, "E72.right", {"start": v(28, 26) * mm, "end": v(28, 30) * mm});
            skLineSegment(sketch, "E73.bottom", {"start": v(39.23, 26) * mm, "end": v(58.23, 26) * mm});
            skLineSegment(sketch, "E73.top", {"start": v(39.23, 30) * mm, "end": v(58.23, 30) * mm});
            skLineSegment(sketch, "E73.left", {"start": v(39.23, 26) * mm, "end": v(39.23, 30) * mm});
            skLineSegment(sketch, "E73.right", {"start": v(58.23, 26) * mm, "end": v(58.23, 30) * mm});
            skLineSegment(sketch, "E74.bottom", {"start": v(71.1, 26) * mm, "end": v(90.1, 26) * mm});
            skLineSegment(sketch, "E74.top", {"start": v(71.1, 30) * mm, "end": v(90.1, 30) * mm});
            skLineSegment(sketch, "E74.left", {"start": v(71.1, 26) * mm, "end": v(71.1, 30) * mm});
            skLineSegment(sketch, "E74.right", {"start": v(90.1, 26) * mm, "end": v(90.1, 30) * mm});
            skSolve(sketch);
        }
        {
            var Q0;
            Q0=makeQuery(id+"F20.imprint","IMPRINT",FACE,{"disambiguationData":[TD([[makeQuery(id+"F20.imprint","IMPRINT",EDGE,{"derivedFrom":sQuery(id+"F20.wireOp",EDGE,"E72.bottom")}),1.0]])]});
            var Q1;
            Q1=makeQuery(id+"F20.imprint","IMPRINT",FACE,{"disambiguationData":[TD([[makeQuery(id+"F20.imprint","IMPRINT",EDGE,{"derivedFrom":sQuery(id+"F20.wireOp",EDGE,"E73.bottom")}),1.0]])]});
            var Q2;
            Q2=makeQuery(id+"F20.imprint","IMPRINT",FACE,{"disambiguationData":[TD([[makeQuery(id+"F20.imprint","IMPRINT",EDGE,{"derivedFrom":sQuery(id+"F20.wireOp",EDGE,"E74.bottom")}),1.0]])]});
            extrude(context, id + "F21", {"entities" : qUnion([Q0, Q1, Q2]), "operationType" : NewBodyOperationType.REMOVE, "oppositeDirection" : true, "depth" : 5 * mm, "offsetDistance" : 25 * mm});
        }
        {
            var Q0;
            Q0=makeQuery(id+"F2.opShell","OFFSET_FACE",FACE,{"disambiguationData":[OSD([sQuery(id+"F0.wireOp",EDGE,"E0.bottom"),sQuery(id+"F0.wireOp",EDGE,"E0.top"),sQuery(id+"F0.wireOp",EDGE,"E0.left"),sQuery(id+"F0.wireOp",EDGE,"E0.right")])]});
            var sketch = newSketch(context, id + "F22", { "sketchPlane" : qUnion([Q0])});
            skLineSegment(sketch, "E75.bottom", {"start": v(-113, 3) * mm, "end": v(-3, 3) * mm});
            skLineSegment(sketch, "E75.top", {"start": v(-113, 142) * mm, "end": v(-3, 142) * mm});
            skLineSegment(sketch, "E75.left", {"start": v(-113, 3) * mm, "end": v(-113, 142) * mm});
            skLineSegment(sketch, "E75.right", {"start": v(-3, 3) * mm, "end": v(-3, 142) * mm});
            skSolve(sketch);
        }
        {
            var Q0;
            {var subQ8=sQuery(id+"F22.wireOp",EDGE,"E75.bottom");Q0=makeQuery(id+"F22.imprint","IMPRINT",FACE,{"disambiguationData":[TD([[makeQuery(id+"F22.imprint","IMPRINT",EDGE,{"derivedFrom":subQ8}),-1.0]])]});}
            extrude(context, id + "F23", {"entities" : qUnion([Q0]), "operationType" : NewBodyOperationType.REMOVE, "oppositeDirection" : true, "depth" : 1.5 * mm, "offsetDistance" : 25 * mm});
        }
        {
            var Q0;
            Q0=makeQuery(id+"F23.boolean.opBoolean","MERGE",FACE,{"derivedFrom":[makeQuery(id+"F2.opShell","OFFSET_FACE",FACE,{"disambiguationData":[OSD([sQuery(id+"F0.wireOp",EDGE,"E0.top")])]}),makeQuery(id+"F23.opExtrude","SWEPT_FACE",FACE,{"disambiguationData":[OSD([sQuery(id+"F22.wireOp",EDGE,"E75.top")])]})]});
            var sketch = newSketch(context, id + "F24", { "sketchPlane" : qUnion([Q0])});
            skLineSegment(sketch, "E76.bottom", {"start": v(-113, 1.5) * mm, "end": v(-3, 1.5) * mm});
            skLineSegment(sketch, "E76.top", {"start": v(-113, 36) * mm, "end": v(-3, 36) * mm});
            skLineSegment(sketch, "E76.left", {"start": v(-113, 1.5) * mm, "end": v(-113, 36) * mm});
            skLineSegment(sketch, "E76.right", {"start": v(-3, 1.5) * mm, "end": v(-3, 36) * mm});
            skSolve(sketch);
        }
        {
            var Q0;
            Q0=makeQuery(id+"F24.imprint","IMPRINT",FACE,{"disambiguationData":[TD([[makeQuery(id+"F24.imprint","IMPRINT",EDGE,{"derivedFrom":sQuery(id+"F24.wireOp",EDGE,"E76.bottom")}),-1.0]])]});
            extrude(context, id + "F25", {"entities" : qUnion([Q0]), "operationType" : NewBodyOperationType.REMOVE, "oppositeDirection" : true, "depth" : 1.5 * mm, "offsetDistance" : 25 * mm});
        }
        {
            var Q0;
            Q0=makeQuery(id+"F25.boolean.opBoolean","MERGE",FACE,{"derivedFrom":[makeQuery(id+"F23.boolean.opBoolean","MERGE",FACE,{"derivedFrom":[makeQuery(id+"F2.opShell","OFFSET_FACE",FACE,{"disambiguationData":[OSD([sQuery(id+"F0.wireOp",EDGE,"E0.right")])]}),makeQuery(id+"F23.opExtrude","SWEPT_FACE",FACE,{"disambiguationData":[OSD([sQuery(id+"F22.wireOp",EDGE,"E75.left")])]})]}),makeQuery(id+"F25.opExtrude","SWEPT_FACE",FACE,{"disambiguationData":[OSD([sQuery(id+"F24.wireOp",EDGE,"E76.left")])]})]});
            var sketch = newSketch(context, id + "F26", { "sketchPlane" : qUnion([Q0])});
            skLineSegment(sketch, "E77.bottom", {"start": v(143.5, 1.5) * mm, "end": v(3, 1.5) * mm});
            skLineSegment(sketch, "E77.top", {"start": v(143.5, 36) * mm, "end": v(3, 36) * mm});
            skLineSegment(sketch, "E77.left", {"start": v(143.5, 1.5) * mm, "end": v(143.5, 36) * mm});
            skLineSegment(sketch, "E77.right", {"start": v(3, 1.5) * mm, "end": v(3, 36) * mm});
            skSolve(sketch);
        }
        {
            var Q0;
            Q0=makeQuery(id+"F26.imprint","IMPRINT",FACE,{"disambiguationData":[TD([[makeQuery(id+"F26.imprint","IMPRINT",EDGE,{"derivedFrom":sQuery(id+"F26.wireOp",EDGE,"E77.bottom")}),1.0]])]});
            extrude(context, id + "F27", {"entities" : qUnion([Q0]), "operationType" : NewBodyOperationType.REMOVE, "oppositeDirection" : true, "depth" : 1.5 * mm, "offsetDistance" : 25 * mm});
        }
        {
            var Q0;
            Q0=makeQuery(id+"F27.boolean.opBoolean","MERGE",FACE,{"derivedFrom":[makeQuery(id+"F23.boolean.opBoolean","MERGE",FACE,{"derivedFrom":[makeQuery(id+"F2.opShell","OFFSET_FACE",FACE,{"disambiguationData":[OSD([sQuery(id+"F0.wireOp",EDGE,"E0.bottom")])]}),makeQuery(id+"F23.opExtrude","SWEPT_FACE",FACE,{"disambiguationData":[OSD([sQuery(id+"F22.wireOp",EDGE,"E75.bottom")])]})]}),makeQuery(id+"F27.opExtrude","SWEPT_FACE",FACE,{"disambiguationData":[OSD([sQuery(id+"F26.wireOp",EDGE,"E77.right")])]})]});
            var sketch = newSketch(context, id + "F28", { "sketchPlane" : qUnion([Q0])});
            skLineSegment(sketch, "E78.bottom", {"start": v(114.5, 1.5) * mm, "end": v(3, 1.5) * mm});
            skLineSegment(sketch, "E78.top", {"start": v(114.5, 36) * mm, "end": v(3, 36) * mm});
            skLineSegment(sketch, "E78.left", {"start": v(114.5, 1.5) * mm, "end": v(114.5, 36) * mm});
            skLineSegment(sketch, "E78.right", {"start": v(3, 1.5) * mm, "end": v(3, 36) * mm});
            skSolve(sketch);
        }
        {
            var Q0;
            Q0=makeQuery(id+"F28.imprint","IMPRINT",FACE,{"disambiguationData":[TD([[makeQuery(id+"F28.imprint","IMPRINT",EDGE,{"derivedFrom":sQuery(id+"F28.wireOp",EDGE,"E78.bottom")}),1.0]])]});
            extrude(context, id + "F29", {"entities" : qUnion([Q0]), "operationType" : NewBodyOperationType.REMOVE, "oppositeDirection" : true, "depth" : 1.5 * mm, "offsetDistance" : 25 * mm});
        }
        {
            var Q0;
            Q0=makeQuery(id+"F29.boolean.opBoolean","MERGE",FACE,{"derivedFrom":[makeQuery(id+"F25.boolean.opBoolean","MERGE",FACE,{"derivedFrom":[makeQuery(id+"F23.boolean.opBoolean","MERGE",FACE,{"derivedFrom":[makeQuery(id+"F2.opShell","OFFSET_FACE",FACE,{"disambiguationData":[OSD([sQuery(id+"F0.wireOp",EDGE,"E0.left")])]}),makeQuery(id+"F23.opExtrude","SWEPT_FACE",FACE,{"disambiguationData":[OSD([sQuery(id+"F22.wireOp",EDGE,"E75.right")])]})]}),makeQuery(id+"F25.opExtrude","SWEPT_FACE",FACE,{"disambiguationData":[OSD([sQuery(id+"F24.wireOp",EDGE,"E76.right")])]})]}),makeQuery(id+"F29.opExtrude","SWEPT_FACE",FACE,{"disambiguationData":[OSD([sQuery(id+"F28.wireOp",EDGE,"E78.right")])]})]});
            var sketch = newSketch(context, id + "F30", { "sketchPlane" : qUnion([Q0])});
            skLineSegment(sketch, "E79.bottom", {"start": v(-1.5, 1.5) * mm, "end": v(-143.5, 1.5) * mm});
            skLineSegment(sketch, "E79.top", {"start": v(-1.5, 36) * mm, "end": v(-143.5, 36) * mm});
            skLineSegment(sketch, "E79.left", {"start": v(-1.5, 1.5) * mm, "end": v(-1.5, 36) * mm});
            skLineSegment(sketch, "E79.right", {"start": v(-143.5, 1.5) * mm, "end": v(-143.5, 36) * mm});
            skSolve(sketch);
        }
        {
            var Q0;
            Q0=makeQuery(id+"F30.imprint","IMPRINT",FACE,{"disambiguationData":[TD([[makeQuery(id+"F30.imprint","IMPRINT",EDGE,{"derivedFrom":sQuery(id+"F30.wireOp",EDGE,"E79.top")}),1.0]])]});
            extrude(context, id + "F31", {"entities" : qUnion([Q0]), "operationType" : NewBodyOperationType.REMOVE, "oppositeDirection" : true, "depth" : 1 * mm, "offsetDistance" : 25 * mm});
        }
    });
